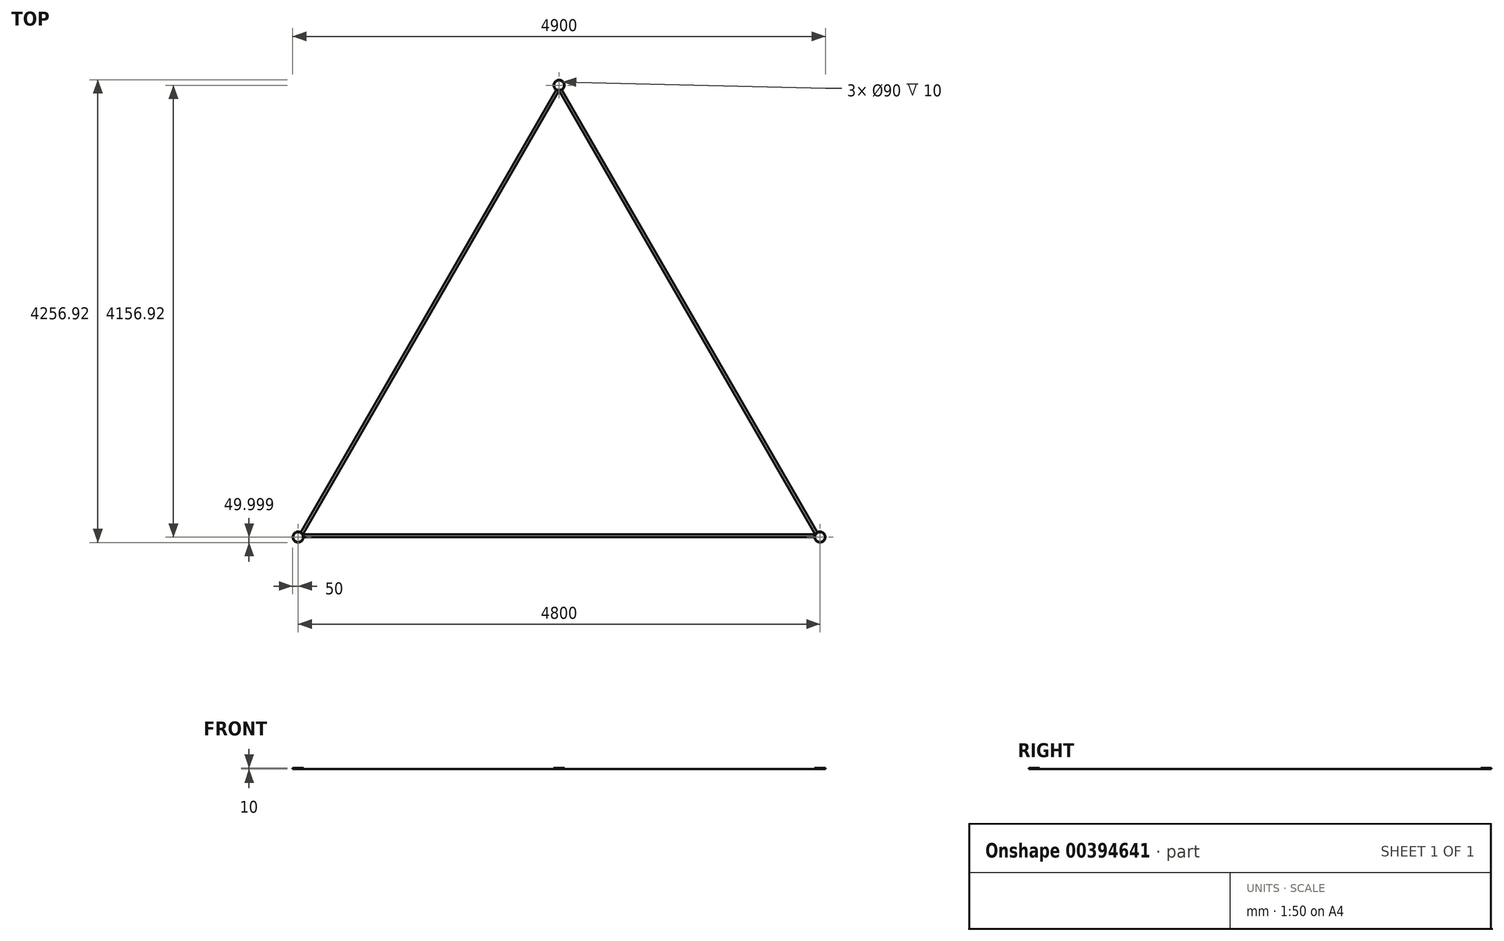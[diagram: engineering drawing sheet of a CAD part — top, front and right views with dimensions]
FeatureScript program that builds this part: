
annotation { "Feature Type Name" : "Feature", "Feature Type Description" : "" }
export const myFeature = defineFeature(function(context is Context, id is Id, definition is map)
    precondition{}
    {
        {
            var Q0;
            Q0=qCreatedBy(makeId("Top.planeOp"),FACE);
            var sketch = newSketch(context, id + "F0", { "sketchPlane" : qUnion([Q0])});
            skCircle(sketch, "E0.cCircle", {"center": v(0, 0) * mm, "radius": 2771.28 * mm, "construction": true});
            skLineSegment(sketch, "E0.0", {"start": v(25, 2727.98) * mm, "end": v(2375, -1342.34) * mm});
            skLineSegment(sketch, "E0.1", {"start": v(2350, -1385.64) * mm, "end": v(-2350, -1385.64) * mm});
            skLineSegment(sketch, "E0.2", {"start": v(-2375, -1342.34) * mm, "end": v(-25, 2727.98) * mm});
            skLineSegment(sketch, "E1.0", {"start": v(-2356.7, -1360.64) * mm, "end": v(0, 2721.28) * mm});
            skLineSegment(sketch, "E1.1", {"start": v(2356.7, -1360.64) * mm, "end": v(-2356.7, -1360.64) * mm});
            skLineSegment(sketch, "E1.2", {"start": v(0, 2721.28) * mm, "end": v(2356.7, -1360.64) * mm});
            skCircle(sketch, "E2", {"center": v(0, 2771.28) * mm, "radius": 50 * mm});
            skCircle(sketch, "E3", {"center": v(0, 2771.28) * mm, "radius": 45 * mm});
            skCircle(sketch, "E4", {"center": v(2400, -1385.64) * mm, "radius": 50 * mm});
            skCircle(sketch, "E5", {"center": v(2400, -1385.64) * mm, "radius": 45 * mm});
            skCircle(sketch, "E6", {"center": v(-2400, -1385.64) * mm, "radius": 50 * mm});
            skCircle(sketch, "E7", {"center": v(-2400, -1385.64) * mm, "radius": 45 * mm});
            skSolve(sketch);
        }
        {
            var Q0;
            Q0=makeQuery(id+"F0.imprint","IMPRINT",FACE,{"disambiguationData":[TD([[makeQuery(id+"F0.imprint","IMPRINT",EDGE,{"derivedFrom":sQuery(id+"F0.wireOp",EDGE,"E7")}),-1.0]])]});
            var Q1;
            Q1=makeQuery(id+"F0.imprint","IMPRINT",FACE,{"disambiguationData":[TD([[makeQuery(id+"F0.imprint","IMPRINT",EDGE,{"derivedFrom":sQuery(id+"F0.wireOp",EDGE,"E5")}),-1.0]])]});
            var Q2;
            Q2=makeQuery(id+"F0.imprint","IMPRINT",FACE,{"disambiguationData":[TD([[makeQuery(id+"F0.imprint","IMPRINT",EDGE,{"derivedFrom":sQuery(id+"F0.wireOp",EDGE,"E3")}),-1.0]])]});
            extrude(context, id + "F1", {"entities" : qUnion([Q0, Q1, Q2]), "depth" : 10 * mm, "offsetDistance" : 25 * mm});
        }
        {
            var Q0;
            {var subQ0=sQuery(id+"F0.wireOp",EDGE,"E0.2");Q0=makeQuery(id+"F0.imprint","IMPRINT",FACE,{"disambiguationData":[TD([[makeQuery(id+"F0.imprint","IMPRINT",EDGE,{"derivedFrom":subQ0}),-1.0]])]});}
            var Q1;
            {var subQ0=sQuery(id+"F0.wireOp",EDGE,"E0.0");Q1=makeQuery(id+"F0.imprint","IMPRINT",FACE,{"disambiguationData":[TD([[makeQuery(id+"F0.imprint","IMPRINT",EDGE,{"derivedFrom":subQ0}),-1.0]])]});}
            var Q2;
            {var subQ0=sQuery(id+"F0.wireOp",EDGE,"E0.1");Q2=makeQuery(id+"F0.imprint","IMPRINT",FACE,{"disambiguationData":[TD([[makeQuery(id+"F0.imprint","IMPRINT",EDGE,{"derivedFrom":subQ0}),-1.0]])]});}
            extrude(context, id + "F2", {"entities" : qUnion([Q0, Q1, Q2]), "depth" : 2 * mm, "offsetDistance" : 25 * mm});
        }
    });
